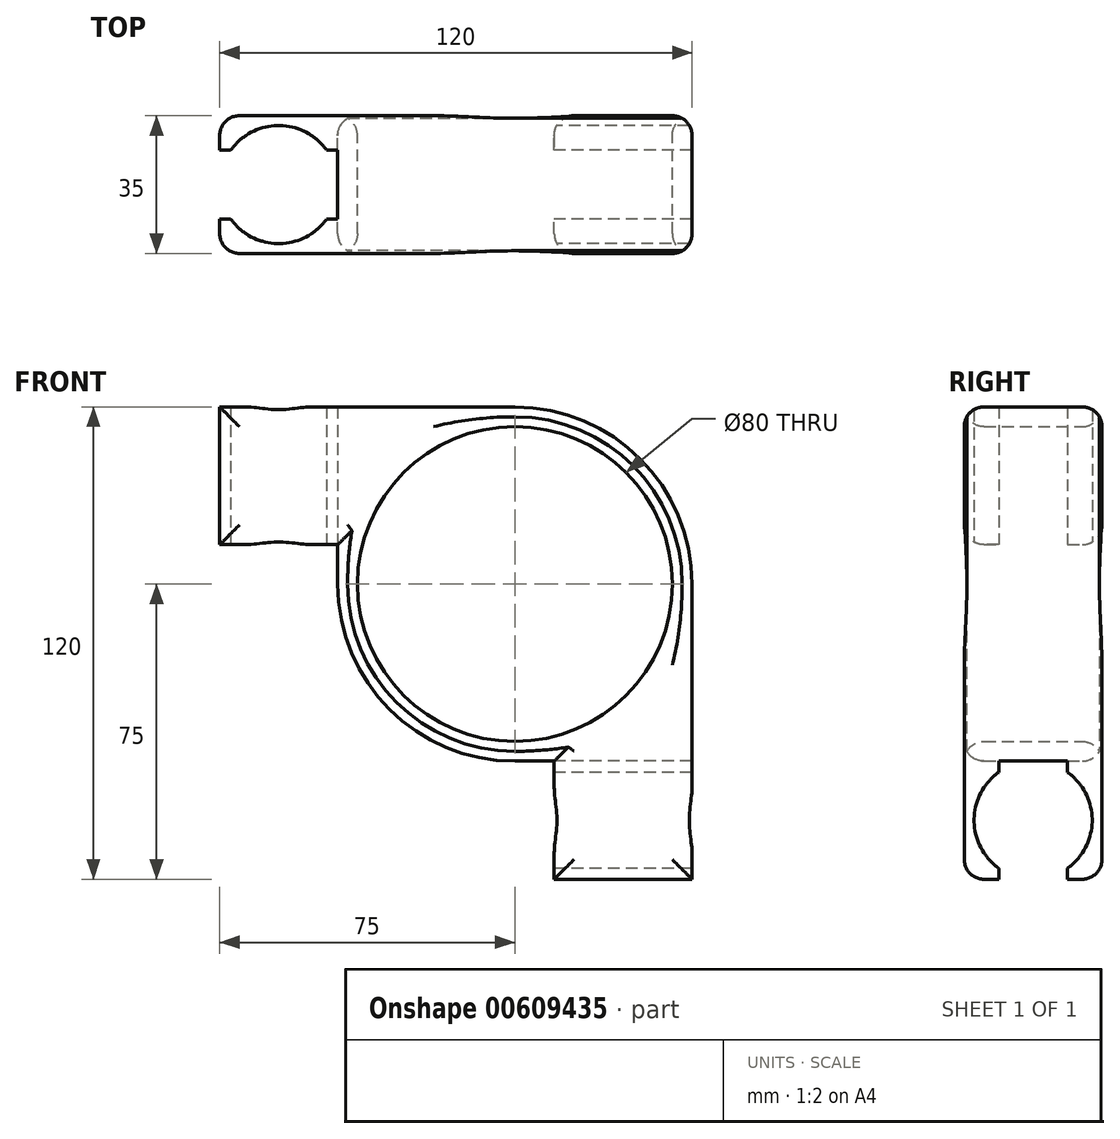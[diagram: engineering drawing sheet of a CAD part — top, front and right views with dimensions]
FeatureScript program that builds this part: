
annotation { "Feature Type Name" : "Feature", "Feature Type Description" : "" }
export const myFeature = defineFeature(function(context is Context, id is Id, definition is map)
    precondition{}
    {
        {
            var Q0;
            Q0=qCreatedBy(makeId("Front.planeOp"),FACE);
            var sketch = newSketch(context, id + "F0", { "sketchPlane" : qUnion([Q0])});
            skLineSegment(sketch, "E0.bottom", {"start": v(-45, 45) * mm, "end": v(0, 45) * mm});
            skLineSegment(sketch, "E0.right", {"start": v(45, 0) * mm, "end": v(45, -45) * mm});
            skCircle(sketch, "E1", {"center": v(0, 0) * mm, "radius": 40 * mm});
            skPoint(sketch, "E2", {"position": v(0, 45) * mm});
            skPoint(sketch, "E3", {"position": v(45, 0) * mm});
            skPoint(sketch, "E4.orphan", {"position": v(45, 45) * mm});
            skArc(sketch, "E5.trimOffspring", {"start": v(45, 0) * mm, "mid": v(31.62, 31.62) * mm, "end": v(0, 45) * mm});
            skLineSegment(sketch, "E6.bottom", {"start": v(0, 45) * mm, "end": v(-45.71, 45) * mm});
            skPoint(sketch, "E6.top.end.orphan", {"position": v(-45, 80.71) * mm});
            skLineSegment(sketch, "E7.top", {"start": v(0, -45) * mm, "end": v(10, -45) * mm});
            skLineSegment(sketch, "E7.left", {"start": v(-45, 10) * mm, "end": v(-45, 0) * mm});
            skArc(sketch, "E8", {"start": v(-45, 0) * mm, "mid": v(-31.82, -31.82) * mm, "end": v(0, -45) * mm});
            skPoint(sketch, "E9.right.end.orphan", {"position": v(45, -80) * mm});
            skArc(sketch, "E10.trimOffspring", {"start": v(45, 0) * mm, "mid": v(31.82, 31.82) * mm, "end": v(0, 45) * mm});
            skLineSegment(sketch, "E11.bottom", {"start": v(-45, 45) * mm, "end": v(-75, 45) * mm});
            skLineSegment(sketch, "E11.top", {"start": v(-45, 10) * mm, "end": v(-75, 10) * mm});
            skLineSegment(sketch, "E11.right", {"start": v(-75, 45) * mm, "end": v(-75, 10) * mm});
            skLineSegment(sketch, "E12.top", {"start": v(45, -75) * mm, "end": v(10, -75) * mm});
            skLineSegment(sketch, "E12.left", {"start": v(45, -45) * mm, "end": v(45, -75) * mm});
            skLineSegment(sketch, "E12.right", {"start": v(10, -45) * mm, "end": v(10, -75) * mm});
            skSolve(sketch);
        }
        {
            var Q0;
            Q0 = qSketchRegion(id + "F0", true);
            extrude(context, id + "F1", {"entities" : qUnion([Q0]), "depth" : 35 * mm, "offsetDistance" : 25 * mm});
        }
        {
            var Q0;
            Q0=qCreatedBy(makeId("Top.planeOp"),FACE);
            var sketch = newSketch(context, id + "F2", { "sketchPlane" : qUnion([Q0])});
            skCircle(sketch, "E13", {"center": v(-60, -17.5) * mm, "radius": 15 * mm});
            skPoint(sketch, "E14.end.orphan", {"position": v(-45, -35) * mm});
            skPoint(sketch, "E15.end.orphan", {"position": v(-37.5, 0) * mm});
            skPoint(sketch, "E16.orphan", {"position": v(0, 0) * mm});
            skPoint(sketch, "E17.end.orphan", {"position": v(-75, 0) * mm});
            skSolve(sketch);
        }
        {
            var Q0;
            Q0=qCreatedBy(makeId("Right.planeOp"),FACE);
            var sketch = newSketch(context, id + "F3", { "sketchPlane" : qUnion([Q0])});
            skLineSegment(sketch, "E18", {"start": v(0, 0) * mm, "end": v(0, 45) * mm});
            skLineSegment(sketch, "E19", {"start": v(0, 45) * mm, "end": v(-35, 45) * mm});
            skLineSegment(sketch, "E20", {"start": v(-35, 45) * mm, "end": v(-17.5, 45) * mm});
            skLineSegment(sketch, "E21", {"start": v(-17.5, 45) * mm, "end": v(-26.25, 45) * mm});
            skLineSegment(sketch, "E22.bottom", {"start": v(-26.25, 45) * mm, "end": v(-8.75, 45) * mm});
            skLineSegment(sketch, "E22.top", {"start": v(-26.25, 10) * mm, "end": v(-8.75, 10) * mm});
            skLineSegment(sketch, "E22.left", {"start": v(-26.25, 45) * mm, "end": v(-26.25, 10) * mm});
            skLineSegment(sketch, "E22.right", {"start": v(-8.75, 45) * mm, "end": v(-8.75, 10) * mm});
            skSolve(sketch);
        }
        {
            var Q0;
            Q0 = qSketchRegion(id + "F3", true);
            extrude(context, id + "F4", {"entities" : qUnion([Q0]), "operationType" : NewBodyOperationType.REMOVE, "oppositeDirection" : true, "depth" : 89 * mm, "offsetDistance" : 25 * mm, "hasSecondDirection" : true, "secondDirectionOppositeDirection" : true, "secondDirectionDepth" : 45 * mm});
        }
        {
            var Q0;
            Q0 = qSketchRegion(id + "F2", true);
            extrude(context, id + "F5", {"entities" : qUnion([Q0]), "operationType" : NewBodyOperationType.REMOVE, "depth" : 52 * mm, "offsetDistance" : 25 * mm});
        }
        {
            var Q0;
            Q0=qCreatedBy(makeId("Top.planeOp"),FACE);
            var sketch = newSketch(context, id + "F6", { "sketchPlane" : qUnion([Q0])});
            skLineSegment(sketch, "E23", {"start": v(0, 0) * mm, "end": v(45, 0) * mm});
            skLineSegment(sketch, "E24", {"start": v(45, 0) * mm, "end": v(45, -35) * mm});
            skLineSegment(sketch, "E25", {"start": v(45, 0) * mm, "end": v(45, -17.5) * mm});
            skLineSegment(sketch, "E26", {"start": v(45, -17.5) * mm, "end": v(45, -8.75) * mm});
            skLineSegment(sketch, "E27.bottom", {"start": v(45, -8.75) * mm, "end": v(10, -8.75) * mm});
            skLineSegment(sketch, "E27.top", {"start": v(45, -26.25) * mm, "end": v(10, -26.25) * mm});
            skLineSegment(sketch, "E27.left", {"start": v(45, -8.75) * mm, "end": v(45, -26.25) * mm});
            skLineSegment(sketch, "E27.right", {"start": v(10, -8.75) * mm, "end": v(10, -26.25) * mm});
            skSolve(sketch);
        }
        {
            var Q0;
            Q0 = qSketchRegion(id + "F6", true);
            extrude(context, id + "F7", {"entities" : qUnion([Q0]), "operationType" : NewBodyOperationType.REMOVE, "oppositeDirection" : true, "depth" : 92 * mm, "offsetDistance" : 25 * mm, "hasSecondDirection" : true, "secondDirectionOppositeDirection" : true, "secondDirectionDepth" : 45 * mm});
        }
        {
            var Q0;
            Q0=qCreatedBy(makeId("Right.planeOp"),FACE);
            var sketch = newSketch(context, id + "F8", { "sketchPlane" : qUnion([Q0])});
            skCircle(sketch, "E28", {"center": v(-17.5, -60) * mm, "radius": 15 * mm});
            skPoint(sketch, "E29.end.orphan", {"position": v(-35, -45) * mm});
            skPoint(sketch, "E30.end.orphan", {"position": v(0, -75) * mm});
            skSolve(sketch);
        }
        {
            var Q0;
            Q0 = qSketchRegion(id + "F8", true);
            extrude(context, id + "F9", {"entities" : qUnion([Q0]), "operationType" : NewBodyOperationType.REMOVE, "depth" : 77 * mm, "offsetDistance" : 25 * mm});
        }
        {
            var Q0;
            Q0=makeQuery(id+"F1.opExtrude","CAP_EDGE",EDGE,{"disambiguationData":[OSD([sQuery(id+"F0.wireOp",EDGE,"E1")])],"isStart":true});
            var Q1;
            Q1=makeQuery(id+"F1.opExtrude","SWEPT_FACE",FACE,{"disambiguationData":[OSD([sQuery(id+"F0.wireOp",EDGE,"E8")])]});
            var Q2;
            Q2=makeQuery(id+"F1.opExtrude","CAP_FACE",FACE,{"disambiguationData":[OSD([sQuery(id+"F0.wireOp",EDGE,"E1"),sQuery(id+"F0.wireOp",EDGE,"E0.bottom"),sQuery(id+"F0.wireOp",EDGE,"E7.top"),sQuery(id+"F0.wireOp",EDGE,"E7.left"),sQuery(id+"F0.wireOp",EDGE,"E0.right"),sQuery(id+"F0.wireOp",EDGE,"E8"),sQuery(id+"F0.wireOp",EDGE,"E10.trimOffspring"),sQuery(id+"F0.wireOp",EDGE,"E11.bottom"),sQuery(id+"F0.wireOp",EDGE,"E11.top"),sQuery(id+"F0.wireOp",EDGE,"E11.right"),sQuery(id+"F0.wireOp",EDGE,"E12.top"),sQuery(id+"F0.wireOp",EDGE,"E12.left"),sQuery(id+"F0.wireOp",EDGE,"E12.right")])],"isStart":true});
            var Q3;
            Q3=makeQuery(id+"F1.opExtrude","CAP_FACE",FACE,{"disambiguationData":[OSD([sQuery(id+"F0.wireOp",EDGE,"E1"),sQuery(id+"F0.wireOp",EDGE,"E0.bottom"),sQuery(id+"F0.wireOp",EDGE,"E7.top"),sQuery(id+"F0.wireOp",EDGE,"E7.left"),sQuery(id+"F0.wireOp",EDGE,"E0.right"),sQuery(id+"F0.wireOp",EDGE,"E8"),sQuery(id+"F0.wireOp",EDGE,"E10.trimOffspring"),sQuery(id+"F0.wireOp",EDGE,"E11.bottom"),sQuery(id+"F0.wireOp",EDGE,"E11.top"),sQuery(id+"F0.wireOp",EDGE,"E11.right"),sQuery(id+"F0.wireOp",EDGE,"E12.top"),sQuery(id+"F0.wireOp",EDGE,"E12.left"),sQuery(id+"F0.wireOp",EDGE,"E12.right")])],"isStart":false});
            fillet(context, id + "F10", {"entities" : qUnion([Q0, Q1, Q2, Q3]), "radius" : 5 * mm, "tangentPropagation" : true, "allowEdgeOverflow" : false});
        }
    });
